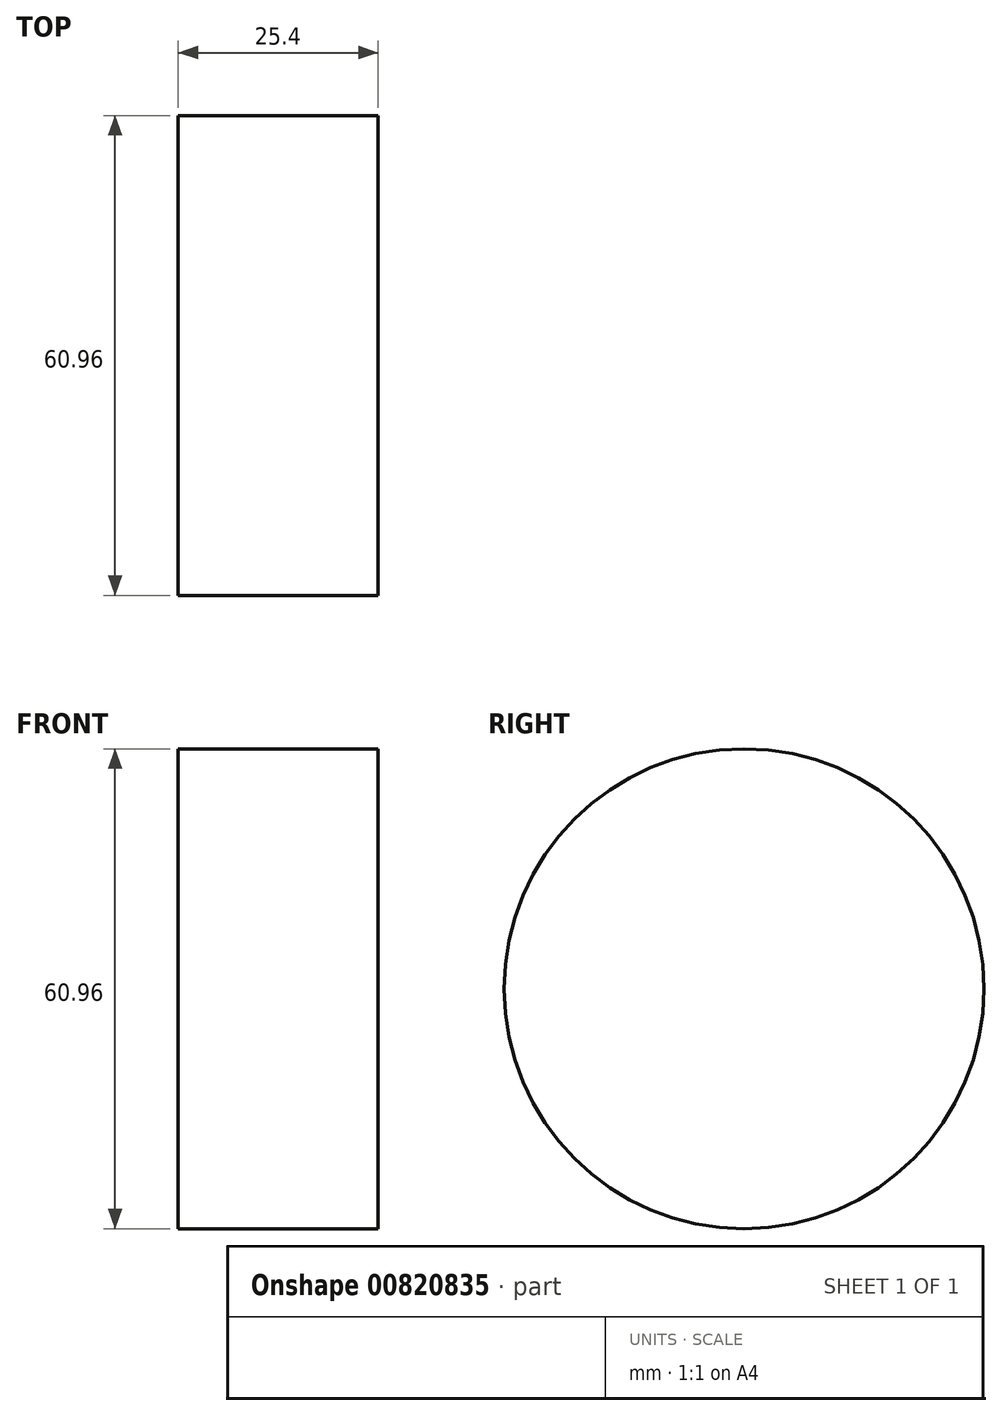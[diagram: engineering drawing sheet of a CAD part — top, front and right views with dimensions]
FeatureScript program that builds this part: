
annotation { "Feature Type Name" : "Feature", "Feature Type Description" : "" }
export const myFeature = defineFeature(function(context is Context, id is Id, definition is map)
    precondition{}
    {
        {
            var Q0;
            Q0=qCreatedBy(makeId("Right.planeOp"),FACE);
            var sketch = newSketch(context, id + "F0", { "sketchPlane" : qUnion([Q0])});
            skCircle(sketch, "E0", {"center": v(59.4, -51.86) * mm, "radius": 30.48 * mm});
            skSolve(sketch);
        }
        {
            var Q0;
            Q0 = qSketchRegion(id + "F0", true);
            extrude(context, id + "F1", {"entities" : qUnion([Q0]), "depth" : 25.4 * mm, "offsetDistance" : 25.4 * mm});
        }
    });
